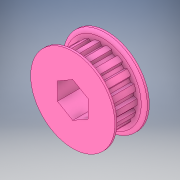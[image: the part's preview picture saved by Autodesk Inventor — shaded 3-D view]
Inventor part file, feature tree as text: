
AUTODESK INVENTOR PART (.ipt)
format: ipt  version: 2017 SP1 (Build 210196100, 196)  size: 232,448 bytes
history: native  units: in
note: dims shown in document units (in); Inventor stores cm internally (conversion verified against a paired STEP export)
features: extrude x2, sketch x2, projected_geometry x1, pattern_circular x1
ambient origin geometry x8: Origin, YZ Plane, XZ Plane, XY Plane, X Axis, Y Axis, Z Axis, Center Point
bodies: Solid1 (feature_tree)
feature tree (6):
  extrude  "Extrusion1"  Depth=0.5in
  extrude  "Extrusion2"  [1 undecoded]
  sketch  "Sketch1"  dims[d0=1.0in d1=0.0in d2=0.5in]
  projected_geometry  "Projected Loop1"
  sketch  "Sketch2"  dims[d3=1.0in d4=0.0in]
  pattern_circular  "CirPattern2"
note: 1 required parameter value undecoded (feature->parameter linkage not recoverable at this tier; creation-order binding heuristic only, values carry confidence <= 0.55)
